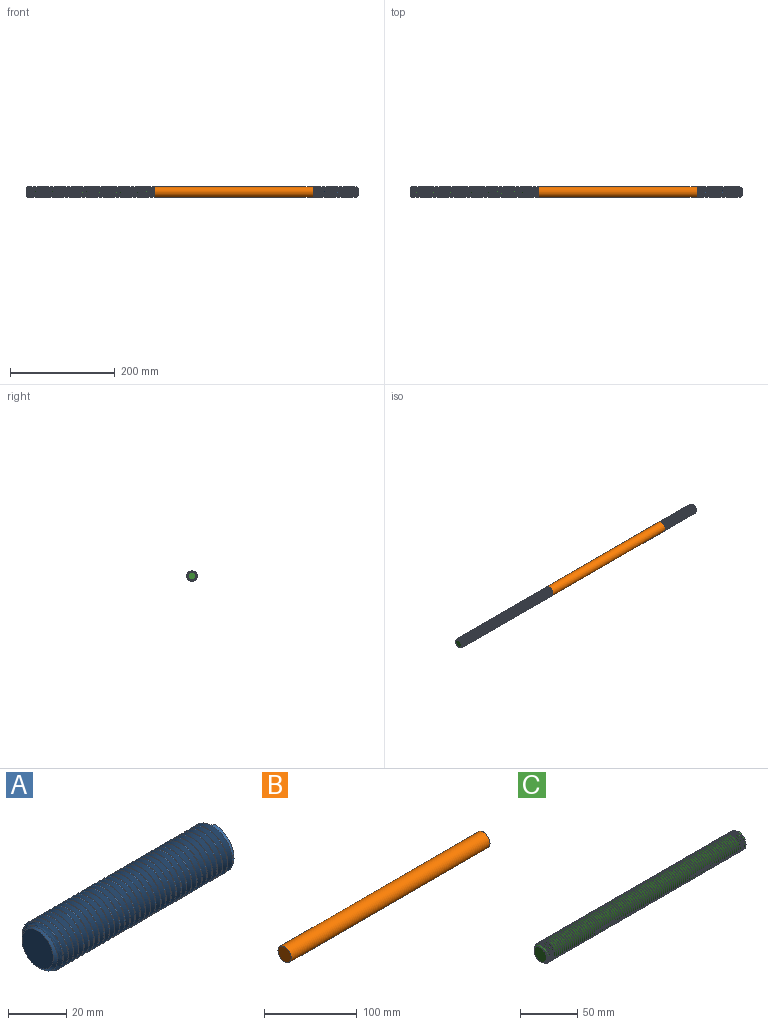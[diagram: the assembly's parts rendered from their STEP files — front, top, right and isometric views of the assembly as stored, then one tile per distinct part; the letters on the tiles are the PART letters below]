
ASSEMBLY  parts=3 mates=2
PART A: 7 faces, bbox 89.8x23.6x20.6 mm
  f0: cylinder r=9.6mm len=84mm, axis (1,0,0), area -590.3mm2, adj f2,f3,f4,f5,f6
  f1: plane 15.2x15.2mm, normal (-1,0,0), area 181.5mm2, adj f3
  f2: plane 20.59x19.82mm, normal (1,0,0), area 266.1mm2, adj f0,f4,f5
  f3: cone r=9.6mm half-angle=45deg, axis (1,0,0), area 86.6mm2, adj f0,f1,f5,f6
  f4: plane 1.89x1.09mm, normal (0,1,0), area 1mm2, adj f0,f2,f6
  f5: bspline ~87.34x22.17mm, area 4018.4mm2, adj f0,f2,f3,f6
  f6: bspline ~87.34x22.17mm, area 4045.4mm2, adj f0,f3,f4,f5
PART B: 3 faces, bbox 304x20x20 mm
  f0: cylinder r=10mm len=304mm, axis (-1,0,0), area 19100.9mm2, adj f1,f2
  f1: plane 20x20mm, normal (1,0,0), area 314.2mm2, adj f0
  f2: plane 20x20mm, normal (-1,0,0), area 314.2mm2, adj f0
PART C: 7 faces, bbox 248.6x23.6x20.6 mm
  f0: cylinder r=9.6mm len=243mm, axis (1,0,0), area -3095.2mm2, adj f2,f3,f4,f5,f6
  f1: plane 15.2x15.2mm, normal (-1,0,0), area 181.5mm2, adj f3
  f2: plane 20.59x19.82mm, normal (1,0,0), area 266.1mm2, adj f0,f4,f5
  f3: cone r=9.6mm half-angle=45deg, axis (1,0,0), area 86.9mm2, adj f0,f1,f5,f6
  f4: plane 1.89x1.09mm, normal (0,1,0), area 1mm2, adj f0,f2,f6
  f5: bspline ~246.09x22.17mm, area 11605.2mm2, adj f0,f2,f3,f6
  f6: bspline ~246.09x22.17mm, area 11579.3mm2, adj f0,f3,f4,f5
PLACE A rot(axis=(0,1,0),180deg) t=(249.7,30.25,-43.56)mm
PLACE B t=(-54.3,30.25,-43.56)mm
PLACE C t=(-54.3,30.25,-43.56)mm
MATE fastened C.f0 <-> B.f0  axis (1,0,0) through (-54.3,30.25,-43.56)mm
MATE fastened A.f0 <-> B.f0  axis (-1,0,0) through (249.7,30.25,-43.56)mm
